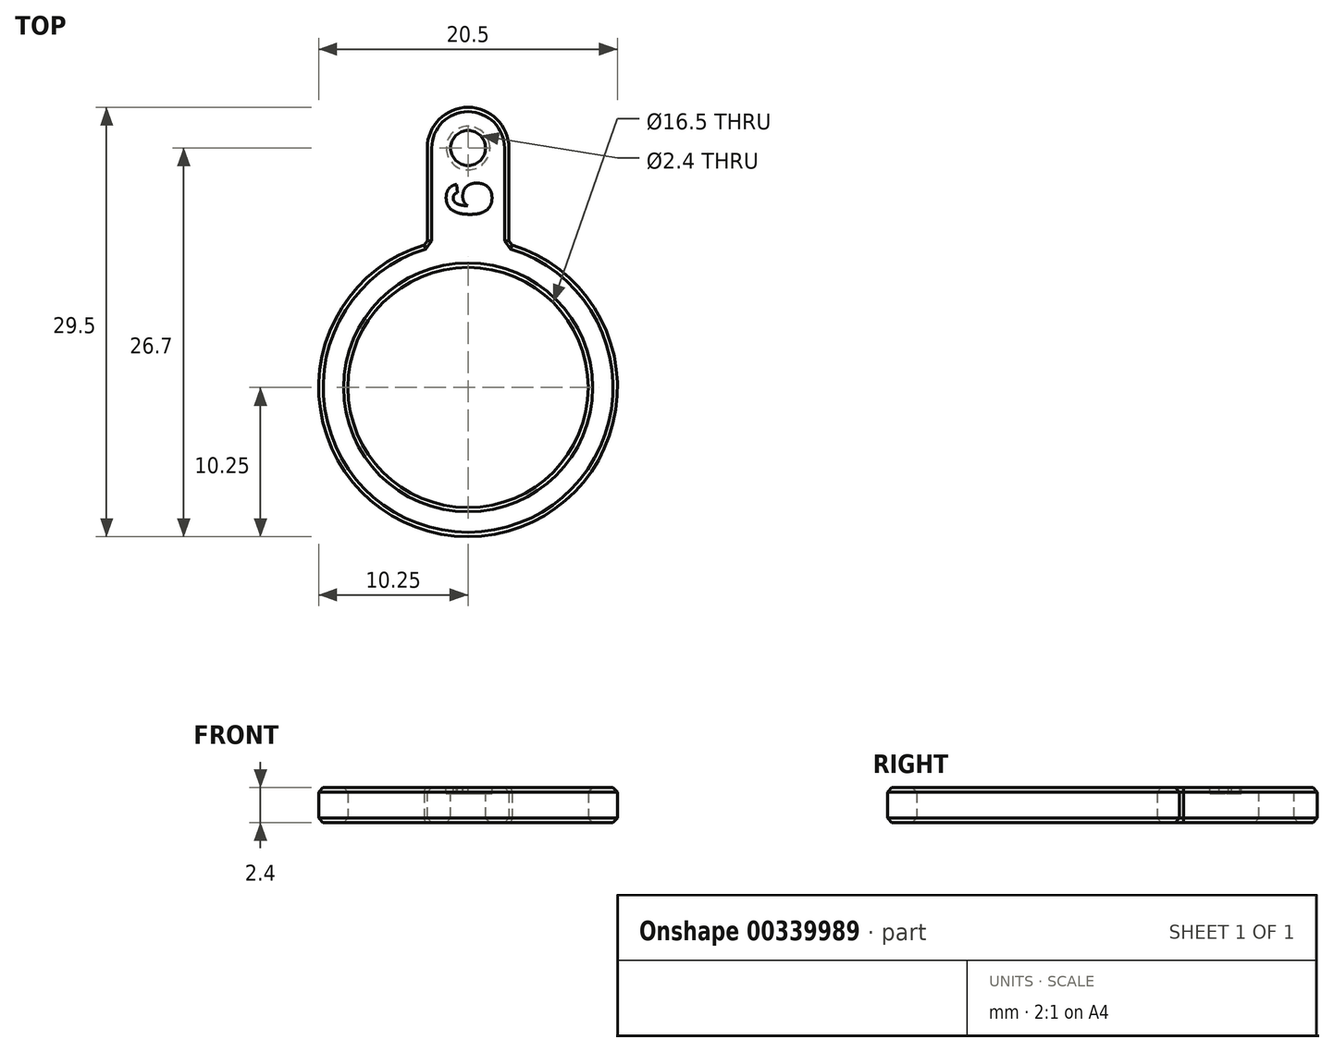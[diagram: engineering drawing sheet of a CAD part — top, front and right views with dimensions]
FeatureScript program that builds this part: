
annotation { "Feature Type Name" : "Feature", "Feature Type Description" : "" }
export const myFeature = defineFeature(function(context is Context, id is Id, definition is map)
    precondition{}
    {
        {
            var Q0;
            Q0=qCreatedBy(makeId("Top.planeOp"),FACE);
            var sketch = newSketch(context, id + "F0", { "sketchPlane" : qUnion([Q0])});
            skCircle(sketch, "E0", {"center": v(0, 0) * mm, "radius": 8.25 * mm});
            skCircle(sketch, "E1", {"center": v(0, 0) * mm, "radius": 10.25 * mm});
            skLineSegment(sketch, "E2.bottom", {"start": v(2.8, 1.25) * mm, "end": v(-2.8, 1.25) * mm});
            skLineSegment(sketch, "E2.top", {"start": v(2.8, 19.25) * mm, "end": v(-2.8, 19.25) * mm});
            skLineSegment(sketch, "E2.left", {"start": v(2.8, 1.25) * mm, "end": v(2.8, 19.25) * mm});
            skLineSegment(sketch, "E2.right", {"start": v(-2.8, 1.25) * mm, "end": v(-2.8, 19.25) * mm});
            skPoint(sketch, "E2.middle", {"position": v(0, 10.25) * mm});
            skSolve(sketch);
        }
        {
            var Q0;
            Q0=qSketchRegion(id+"F0",true);
            extrude(context, id + "F1", {"entities" : qUnion([Q0]), "depth" : 2.4 * mm});
        }
        {
            var Q0;
            Q0=makeQuery(id+"F1.opExtrude","SWEPT_EDGE",EDGE,{"disambiguationData":[OSD([sQuery(id+"F0.wireOp",EDGE,"E2.top"),sQuery(id+"F0.wireOp",EDGE,"E2.right")])]});
            var Q1;
            Q1=makeQuery(id+"F1.opExtrude","SWEPT_EDGE",EDGE,{"disambiguationData":[OSD([sQuery(id+"F0.wireOp",EDGE,"E2.top"),sQuery(id+"F0.wireOp",EDGE,"E2.left")])]});
            fillet(context, id + "F2", {"entities" : qUnion([Q0, Q1]), "radius" : 2.8 * mm, "tangentPropagation" : true, "allowEdgeOverflow" : false});
        }
        {
            var Q0;
            Q0=makeQuery(id+"F1.opExtrude","CAP_FACE",FACE,{"disambiguationData":[OSD([sQuery(id+"F0.wireOp",EDGE,"E0"),sQuery(id+"F0.wireOp",EDGE,"E1"),sQuery(id+"F0.wireOp",EDGE,"E2.top"),sQuery(id+"F0.wireOp",EDGE,"E2.left"),sQuery(id+"F0.wireOp",EDGE,"E2.right")])],"isStart":false});
            var sketch = newSketch(context, id + "F3", { "sketchPlane" : qUnion([Q0])});
            skCircle(sketch, "E3", {"center": v(0, 16.45) * mm, "radius": 1.2 * mm});
            skSolve(sketch);
        }
        {
            var Q0;
            Q0=qSketchRegion(id+"F3",true);
            extrude(context, id + "F4", {"entities" : qUnion([Q0]), "operationType" : NewBodyOperationType.REMOVE, "oppositeDirection" : true, "depth" : 25 * mm});
        }
        {
            var Q0;
            Q0=makeQuery(id+"F4.boolean.opBoolean","COPY",EDGE,{"derivedFrom":makeQuery(id+"F4.opExtrude","CAP_EDGE",EDGE,{"disambiguationData":[OSD([sQuery(id+"F3.wireOp",EDGE,"E3")])],"isStart":true})});
            var Q1;
            Q1=makeQuery(id+"F4.boolean.opBoolean","INTERSECT",EDGE,{"derivedFrom":[makeQuery(id+"F1.opExtrude","CAP_FACE",FACE,{"disambiguationData":[OSD([sQuery(id+"F0.wireOp",EDGE,"E0"),sQuery(id+"F0.wireOp",EDGE,"E1"),sQuery(id+"F0.wireOp",EDGE,"E2.top"),sQuery(id+"F0.wireOp",EDGE,"E2.left"),sQuery(id+"F0.wireOp",EDGE,"E2.right")])],"isStart":true}),makeQuery(id+"F4.opExtrude","SWEPT_FACE",FACE,{"disambiguationData":[OSD([sQuery(id+"F3.wireOp",EDGE,"E3")])]})]});
            var Q2;
            {var subQ0=sQuery(id+"F0.wireOp",EDGE,"E2.right");var subQ1=sQuery(id+"F0.wireOp",EDGE,"E2.top");Q2=makeQuery(id+"F2.opFillet","BLEND_EDGE",EDGE,{"blendedFrom":[makeQuery(id+"F1.opExtrude","SWEPT_EDGE",EDGE,{"disambiguationData":[OSD([subQ1,subQ0])]}),makeQuery(id+"F1.opExtrude","CAP_FACE",FACE,{"disambiguationData":[OSD([sQuery(id+"F0.wireOp",EDGE,"E0"),sQuery(id+"F0.wireOp",EDGE,"E1"),subQ1,sQuery(id+"F0.wireOp",EDGE,"E2.left"),subQ0])],"isStart":true})],"blendedInto":[makeQuery(id+"F1.opExtrude","CAP_FACE",FACE,{"disambiguationData":[OSD([sQuery(id+"F0.wireOp",EDGE,"E0"),sQuery(id+"F0.wireOp",EDGE,"E1"),subQ1,sQuery(id+"F0.wireOp",EDGE,"E2.left"),subQ0])],"isStart":true})]});}
            var Q3;
            {var subQ0=sQuery(id+"F0.wireOp",EDGE,"E2.right");var subQ1=sQuery(id+"F0.wireOp",EDGE,"E2.top");Q3=makeQuery(id+"F2.opFillet","BLEND_EDGE",EDGE,{"blendedFrom":[makeQuery(id+"F1.opExtrude","SWEPT_EDGE",EDGE,{"disambiguationData":[OSD([subQ1,subQ0])]}),makeQuery(id+"F1.opExtrude","CAP_FACE",FACE,{"disambiguationData":[OSD([sQuery(id+"F0.wireOp",EDGE,"E0"),sQuery(id+"F0.wireOp",EDGE,"E1"),subQ1,sQuery(id+"F0.wireOp",EDGE,"E2.left"),subQ0])],"isStart":false})],"blendedInto":[makeQuery(id+"F1.opExtrude","CAP_FACE",FACE,{"disambiguationData":[OSD([sQuery(id+"F0.wireOp",EDGE,"E0"),sQuery(id+"F0.wireOp",EDGE,"E1"),subQ1,sQuery(id+"F0.wireOp",EDGE,"E2.left"),subQ0])],"isStart":false})]});}
            var Q4;
            Q4=makeQuery(id+"F1.opExtrude","CAP_EDGE",EDGE,{"disambiguationData":[OSD([sQuery(id+"F0.wireOp",EDGE,"E1")])],"isStart":false});
            var Q5;
            Q5=makeQuery(id+"F1.opExtrude","CAP_EDGE",EDGE,{"disambiguationData":[OSD([sQuery(id+"F0.wireOp",EDGE,"E1")])],"isStart":true});
            var Q6;
            Q6=makeQuery(id+"F1.opExtrude","SWEPT_EDGE",EDGE,{"disambiguationData":[OSD([sQuery(id+"F0.wireOp",EDGE,"E1"),sQuery(id+"F0.wireOp",EDGE,"E2.left")])]});
            var Q7;
            Q7=makeQuery(id+"F1.opExtrude","SWEPT_EDGE",EDGE,{"disambiguationData":[OSD([sQuery(id+"F0.wireOp",EDGE,"E1"),sQuery(id+"F0.wireOp",EDGE,"E2.right")])]});
            var Q8;
            Q8=makeQuery(id+"F1.opExtrude","CAP_EDGE",EDGE,{"disambiguationData":[OSD([sQuery(id+"F0.wireOp",EDGE,"E0")])],"isStart":true});
            var Q9;
            Q9=makeQuery(id+"F1.opExtrude","CAP_EDGE",EDGE,{"disambiguationData":[OSD([sQuery(id+"F0.wireOp",EDGE,"E0")])],"isStart":false});
            chamfer(context, id + "F5", {"entities" : qUnion([Q0, Q1, Q2, Q3, Q4, Q5, Q6, Q7, Q8, Q9]), "width" : 0.3 * mm, "tangentPropagation" : true});
        }
        {
            var Q0;
            Q0=makeQuery(id+"F1.opExtrude","CAP_FACE",FACE,{"disambiguationData":[OSD([sQuery(id+"F0.wireOp",EDGE,"E0"),sQuery(id+"F0.wireOp",EDGE,"E1"),sQuery(id+"F0.wireOp",EDGE,"E2.top"),sQuery(id+"F0.wireOp",EDGE,"E2.left"),sQuery(id+"F0.wireOp",EDGE,"E2.right")])],"isStart":false});
            var sketch = newSketch(context, id + "F6", { "sketchPlane" : qUnion([Q0])});
            skText(sketch, "E4", { "text": "6", "fontName": "Arimo-Bold.ttf"});
            skLineSegment(sketch, "E5", {"start": v(0, 11.73) * mm, "end": v(0, 0) * mm});
            skPoint(sketch, "E5.endSnap0", {"position": v(0, 11.73) * mm});
            const initialGuessF6  = {"E4": [0.0016, 0.01173, 0, 1, 0.0032]};
            skSetInitialGuess(sketch, initialGuessF6);
            skSolve(sketch);
        }
        {
            var Q0;
            Q0=qSketchRegion(id+"F6",true);
            var Q1;
            Q1=makeQuery(id+"F6.imprint","IMPRINT",FACE,{"disambiguationData":[TD([[makeQuery(id+"F6.imprint","IMPRINT",EDGE,{"derivedFrom":sQuery(id+"F6.wireOp",EDGE,"E4.sketch_text.stroke-16")}),1.0]])]});
            extrude(context, id + "F7", {"entities" : qUnion([Q0, Q1]), "operationType" : NewBodyOperationType.REMOVE, "oppositeDirection" : true, "depth" : 0.4 * mm});
        }
    });
